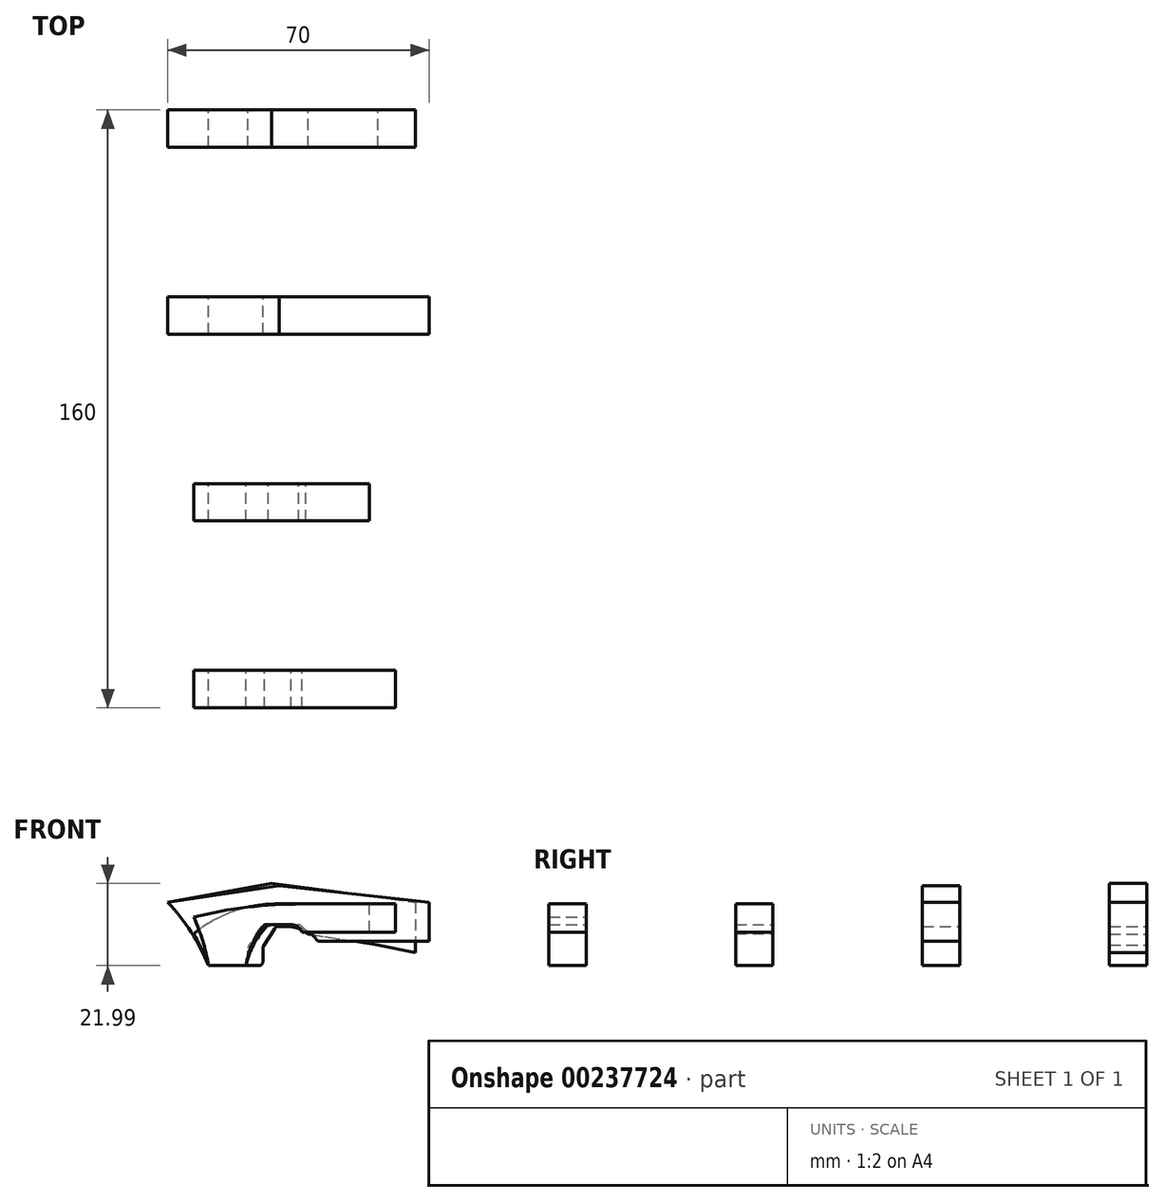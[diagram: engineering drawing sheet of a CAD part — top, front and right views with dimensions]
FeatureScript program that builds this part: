
annotation { "Feature Type Name" : "Feature", "Feature Type Description" : "" }
export const myFeature = defineFeature(function(context is Context, id is Id, definition is map)
    precondition{}
    {
        {
            var Q0;
            Q0=qCreatedBy(makeId("Front.planeOp"),FACE);
            var sketch = newSketch(context, id + "F0", { "sketchPlane" : qUnion([Q0])});
            skLineSegment(sketch, "E0", {"start": v(0, 0) * mm, "end": v(9.5, 0) * mm});
            skPoint(sketch, "E1", {"position": v(-11, 17) * mm});
            skArc(sketch, "E2", {"start": v(0, 0) * mm, "mid": v(-4.71, 9.01) * mm, "end": v(-11, 17) * mm});
            skLineSegment(sketch, "E3", {"start": v(-11, 17) * mm, "end": v(55.3, 17) * mm, "construction": true});
            skLineSegment(sketch, "E4", {"start": v(21, 10.48) * mm, "end": v(14.55, 10.48) * mm});
            skLineSegment(sketch, "E5", {"start": v(10.5, 1) * mm, "end": v(10.5, 4.7) * mm});
            skLineSegment(sketch, "E6", {"start": v(13.7, 10.02) * mm, "end": v(10.66, 5.25) * mm});
            skArc(sketch, "E7", {"start": v(26.27, 8.64) * mm, "mid": v(23.8, 10) * mm, "end": v(21, 10.48) * mm});
            skPoint(sketch, "E8.visualSharp", {"position": v(14, 10.48) * mm});
            skArc(sketch, "E8.filletArc", {"start": v(14.55, 10.48) * mm, "mid": v(14.07, 10.35) * mm, "end": v(13.7, 10.02) * mm});
            skPoint(sketch, "E9.visualSharp", {"position": v(10.5, 5) * mm});
            skArc(sketch, "E9.filletArc", {"start": v(10.66, 5.25) * mm, "mid": v(10.54, 4.99) * mm, "end": v(10.5, 4.7) * mm});
            skPoint(sketch, "E10.visualSharp", {"position": v(10.5, 0) * mm});
            skArc(sketch, "E10.filletArc", {"start": v(9.5, 0) * mm, "mid": v(10.2, 0.3) * mm, "end": v(10.5, 1) * mm});
            skArc(sketch, "E11.filletArc", {"start": v(26.27, 8.64) * mm, "mid": v(26.42, 8.55) * mm, "end": v(26.58, 8.48) * mm});
            skLineSegment(sketch, "E12", {"start": v(55.3, 17) * mm, "end": v(55.3, 3.48) * mm});
            skLineSegment(sketch, "E13", {"start": v(55.3, 3.48) * mm, "end": v(45.3, 5.48) * mm});
            skLineSegment(sketch, "E14", {"start": v(26.58, 8.48) * mm, "end": v(45.3, 5.48) * mm});
            skLineSegment(sketch, "E15", {"start": v(-11, 17) * mm, "end": v(16.9, 22) * mm});
            skLineSegment(sketch, "E16", {"start": v(16.9, 22) * mm, "end": v(55.3, 17) * mm});
            skSolve(sketch);
        }
        {
            var Q0;
            Q0=makeQuery(id+"F0.imprint","IMPRINT",FACE,{"disambiguationData":[TD([[makeQuery(id+"F0.imprint","IMPRINT",EDGE,{"derivedFrom":sQuery(id+"F0.wireOp",EDGE,"E0")}),1.0]])]});
            extrude(context, id + "F1", {"entities" : qUnion([Q0]), "depth" : 10 * mm});
        }
        {
            var Q0;
            Q0=qCreatedBy(makeId("Front.planeOp"),FACE);
            cPlane(context, id + "F2", {"entities" : qUnion([Q0]), "cplaneType" : CPlaneType.OFFSET, "offset" : 50 * mm, "width" : 150 * mm, "height" : 150 * mm});
        }
        {
            var Q0;
            Q0=qCreatedBy(id+"F2.planeOp",FACE);
            var sketch = newSketch(context, id + "F3", { "sketchPlane" : qUnion([Q0])});
            skLineSegment(sketch, "E17", {"start": v(0, 0) * mm, "end": v(13.5, 0) * mm});
            skPoint(sketch, "E18", {"position": v(-11, 17) * mm});
            skArc(sketch, "E19", {"start": v(0, 0) * mm, "mid": v(-4.71, 9.01) * mm, "end": v(-11, 17) * mm});
            skLineSegment(sketch, "E20", {"start": v(-11, 17) * mm, "end": v(59, 17) * mm, "construction": true});
            skLineSegment(sketch, "E21", {"start": v(59, 17) * mm, "end": v(59, 6.48) * mm});
            skLineSegment(sketch, "E22", {"start": v(14.5, 1) * mm, "end": v(14.5, 4.7) * mm});
            skLineSegment(sketch, "E23", {"start": v(14.66, 5.25) * mm, "end": v(17.7, 10.02) * mm});
            skLineSegment(sketch, "E24", {"start": v(18.55, 10.48) * mm, "end": v(22, 10.48) * mm});
            skArc(sketch, "E25", {"start": v(28.93, 6.9) * mm, "mid": v(25.9, 9.53) * mm, "end": v(22, 10.48) * mm});
            skLineSegment(sketch, "E26", {"start": v(59, 6.48) * mm, "end": v(29.75, 6.48) * mm});
            skPoint(sketch, "E27.visualSharp", {"position": v(18, 10.48) * mm});
            skArc(sketch, "E27.filletArc", {"start": v(18.55, 10.48) * mm, "mid": v(18.07, 10.35) * mm, "end": v(17.7, 10.02) * mm});
            skPoint(sketch, "E28.visualSharp", {"position": v(14.5, 5) * mm});
            skArc(sketch, "E28.filletArc", {"start": v(14.66, 5.25) * mm, "mid": v(14.54, 4.99) * mm, "end": v(14.5, 4.7) * mm});
            skPoint(sketch, "E29.visualSharp", {"position": v(29.21, 6.48) * mm});
            skArc(sketch, "E29.filletArc", {"start": v(28.93, 6.9) * mm, "mid": v(29.29, 6.59) * mm, "end": v(29.75, 6.48) * mm});
            skPoint(sketch, "E30.visualSharp", {"position": v(14.5, 0) * mm});
            skArc(sketch, "E30.filletArc", {"start": v(13.5, 0) * mm, "mid": v(14.2, 0.3) * mm, "end": v(14.5, 1) * mm});
            skLineSegment(sketch, "E31", {"start": v(-11, 17) * mm, "end": v(18.85, 21.4) * mm});
            skLineSegment(sketch, "E32", {"start": v(18.85, 21.4) * mm, "end": v(59, 17) * mm});
            skSolve(sketch);
        }
        {
            var Q0;
            Q0=makeQuery(id+"F3.imprint","IMPRINT",FACE,{"disambiguationData":[TD([[makeQuery(id+"F3.imprint","IMPRINT",EDGE,{"derivedFrom":sQuery(id+"F3.wireOp",EDGE,"E17")}),1.0]])]});
            extrude(context, id + "F4", {"entities" : qUnion([Q0]), "depth" : 10 * mm});
        }
        {
            var Q0;
            Q0=qCreatedBy(id+"F2.planeOp",FACE);
            cPlane(context, id + "F5", {"entities" : qUnion([Q0]), "cplaneType" : CPlaneType.OFFSET, "offset" : 50 * mm, "width" : 150 * mm, "height" : 150 * mm});
        }
        {
            var Q0;
            Q0=qCreatedBy(id+"F5.planeOp",FACE);
            var sketch = newSketch(context, id + "F6", { "sketchPlane" : qUnion([Q0])});
            skPoint(sketch, "E33", {"position": v(-4, 8.5) * mm});
            skLineSegment(sketch, "E34", {"start": v(0, 0) * mm, "end": v(10, 0) * mm});
            skPoint(sketch, "E35", {"position": v(16, 11) * mm});
            skArc(sketch, "E36", {"start": v(0, 0) * mm, "mid": v(-1.82, 4.34) * mm, "end": v(-4, 8.5) * mm});
            skArc(sketch, "E37", {"start": v(16, 11) * mm, "mid": v(12.2, 5.94) * mm, "end": v(10, 0) * mm});
            skPoint(sketch, "E38", {"position": v(26, 9) * mm});
            skLineSegment(sketch, "E39", {"start": v(26, 9) * mm, "end": v(43, 9) * mm});
            skLineSegment(sketch, "E40", {"start": v(16, 11) * mm, "end": v(24.1, 11) * mm});
            skArc(sketch, "E41", {"start": v(26, 9) * mm, "mid": v(25.25, 10.2) * mm, "end": v(24.1, 11) * mm});
            skLineSegment(sketch, "E42", {"start": v(43, 9) * mm, "end": v(43, 16.5) * mm});
            skLineSegment(sketch, "E43", {"start": v(43, 16.5) * mm, "end": v(18.27, 16.5) * mm});
            skArc(sketch, "E44", {"start": v(18.27, 16.5) * mm, "mid": v(6.44, 14.44) * mm, "end": v(-4, 8.5) * mm});
            skSolve(sketch);
        }
        {
            var Q0;
            Q0 = qSketchRegion(id + "F6", true);
            extrude(context, id + "F7", {"entities" : qUnion([Q0]), "depth" : 10 * mm});
        }
        {
            var Q0;
            Q0=qCreatedBy(id+"F5.planeOp",FACE);
            cPlane(context, id + "F8", {"entities" : qUnion([Q0]), "cplaneType" : CPlaneType.OFFSET, "offset" : 50 * mm, "width" : 150 * mm, "height" : 150 * mm});
        }
        {
            var Q0;
            Q0=qCreatedBy(id+"F8.planeOp",FACE);
            var sketch = newSketch(context, id + "F9", { "sketchPlane" : qUnion([Q0])});
            skPoint(sketch, "E45", {"position": v(-4, 13) * mm});
            skArc(sketch, "E46", {"start": v(0, 0) * mm, "mid": v(-1.6, 6.62) * mm, "end": v(-4, 13) * mm});
            skLineSegment(sketch, "E47", {"start": v(0, 0) * mm, "end": v(10, 0) * mm});
            skPoint(sketch, "E48", {"position": v(15, 11) * mm});
            skArc(sketch, "E49", {"start": v(15, 11) * mm, "mid": v(11.73, 5.85) * mm, "end": v(10, 0) * mm});
            skLineSegment(sketch, "E50", {"start": v(15, 11) * mm, "end": v(25, 11) * mm});
            skLineSegment(sketch, "E51", {"start": v(25, 11) * mm, "end": v(25, 9) * mm});
            skLineSegment(sketch, "E52", {"start": v(25, 9) * mm, "end": v(50, 9) * mm});
            skLineSegment(sketch, "E53", {"start": v(50, 9) * mm, "end": v(50, 16.5) * mm});
            skLineSegment(sketch, "E54", {"start": v(50, 16.5) * mm, "end": v(25, 16.5) * mm});
            skLineSegment(sketch, "E55", {"start": v(25, 16.5) * mm, "end": v(25, 11) * mm});
            skArc(sketch, "E56", {"start": v(25, 16.5) * mm, "mid": v(10.4, 15.62) * mm, "end": v(-4, 13) * mm});
            skPoint(sketch, "E57", {"position": v(22, 11) * mm});
            skArc(sketch, "E58", {"start": v(25, 9) * mm, "mid": v(23.78, 10.42) * mm, "end": v(22, 11) * mm});
            skSolve(sketch);
        }
        {
            var Q0;
            Q0 = qSketchRegion(id + "F9", true);
            extrude(context, id + "F10", {"entities" : qUnion([Q0]), "depth" : 10 * mm});
        }
    });
